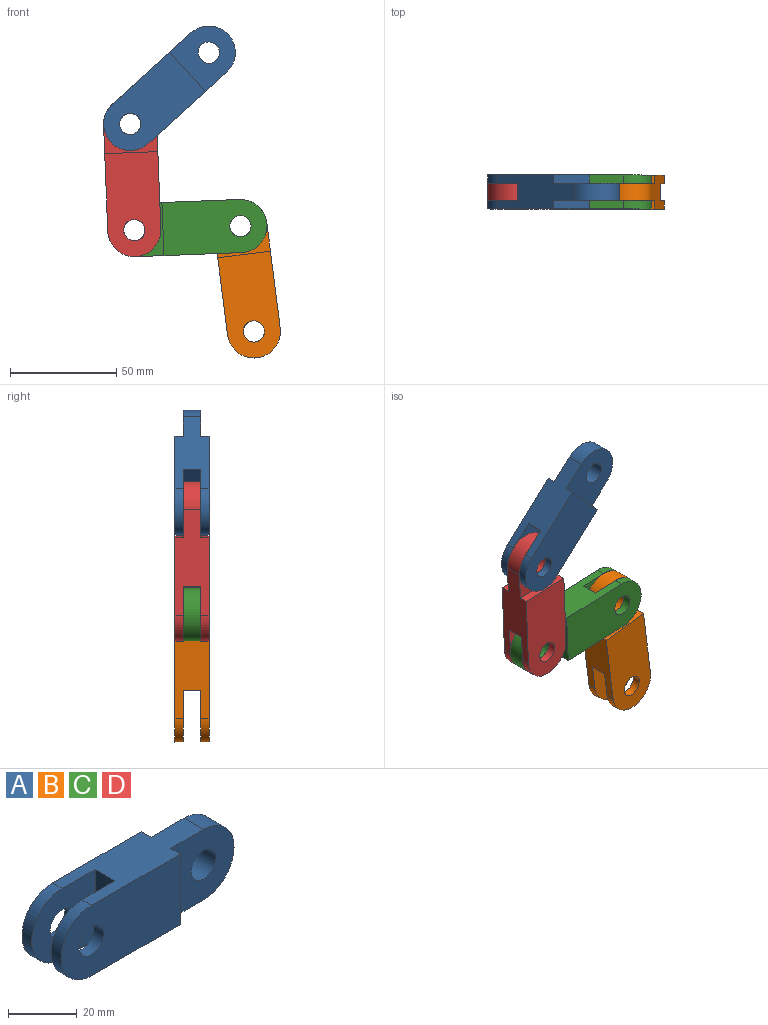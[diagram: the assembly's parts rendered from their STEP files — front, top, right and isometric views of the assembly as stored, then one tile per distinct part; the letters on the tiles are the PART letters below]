
ASSEMBLY  parts=4 mates=3
PART A: 17 faces, bbox 75x16x25 mm
  f0: plane 50x16mm, normal (0,0,-1), area 584mm2, adj f1,f2,f4,f6,f8,f9,f10,f11
  f1: cylinder r=12.5mm len=25mm, axis (0,-1,0), area 157.1mm2, adj f0,f3,f8,f14
  f2: cylinder r=12.5mm len=25mm, axis (0,-1,0), area 157.1mm2, adj f0,f3,f6,f13
  f3: plane 50x16mm, normal (0,0,1), area 584mm2, adj f1,f2,f4,f6,f8,f9,f10,f11
  f4: cylinder r=12.5mm len=25mm, axis (0,-1,0), area 314.2mm2, adj f0,f3,f9,f11
  f5: cylinder r=5mm len=10mm, axis (0,-1,0), area 125.7mm2, adj f6,f13
  f6: plane 49x25mm, normal (0,-1,0), area 1079.4mm2, adj f0,f2,f3,f5,f10
  f7: cylinder r=5mm len=10mm, axis (0,-1,0), area 125.7mm2, adj f8,f14
  f8: plane 49x25mm, normal (0,1,0), area 1079.4mm2, adj f0,f1,f3,f7,f12
  f9: plane 26x25mm, normal (0,-1,0), area 504.4mm2, adj f0,f3,f4,f10,f16
  f10: plane 25x4mm, normal (1,0,0), area 100mm2, adj f0,f3,f6,f9
  f11: plane 26x25mm, normal (0,1,0), area 504.4mm2, adj f0,f3,f4,f12,f16
  f12: plane 25x4mm, normal (1,0,0), area 100mm2, adj f0,f3,f8,f11
  f13: plane 26x25mm, normal (0,1,0), area 504.4mm2, adj f0,f2,f3,f5,f15
  f14: plane 26x25mm, normal (0,-1,0), area 504.4mm2, adj f0,f1,f3,f7,f15
  f15: plane 25x8mm, normal (-1,0,0), area 200mm2, adj f0,f3,f13,f14
  f16: cylinder r=5mm len=10mm, axis (0,-1,0), area 251.3mm2, adj f9,f11
PART B: same geometry as A
PART C: same geometry as A
PART D: same geometry as A
PLACE A rot(axis=(0,-1,0),42.2deg) t=(-1.04,-9.75,48.58)mm
PLACE B rot(axis=(0,-1,0),97.2deg) t=(57.18,-9.75,-49.03)mm
PLACE C rot(axis=(0,1,0),177.8deg) t=(50.88,-9.75,0.58)mm
PLACE D rot(axis=(0,-1,0),92.2deg) t=(0.92,-9.75,-1.38)mm
MATE revolute D.f1 <-> C.f4  axis (0,1,0) through (0.92,-13.75,-1.38)mm
MATE revolute A.f1 <-> D.f4  axis (0,1,0) through (-1.04,-13.75,48.58)mm
MATE revolute C.f1 <-> B.f4  axis (0,1,0) through (50.88,-13.75,0.58)mm
